# Revit family: EC-8-TY4232_Metric
name_source: partatom
category: Sprinklers
units: mm (PartAtom-declared; Revit-internal decimal feet)

## family parameters
Always vertical = Yes
Cut with Voids When Loaded = No
Maintain Annotation Orientation = No
OmniClass Number = 23.65.70.17.11.24
OmniClass Title = Fire Fighting Sprinkler Heads
Part Type = Normal
Room Calculation Point = No
Round Connector Dimension = Use Diameter
Shared = No
Work Plane-Based = No

## types (6) — shared parameters
COBie = Yes
COBie.Component.Name = Sprinklers:Pendent_SIN
COBie.Type = Yes
COBie.Type.AssetType = Fixed
COBie.Type.Category = Pr_70_55_97_84:Sprinklers
COBie.Type.DurationUnit = year
COBie.Type.Manufacturer = Tyco Fire Protection Products
COBie.Type.Material = Bronze
COBie.Type.Shape = Cylinder
COBie.Type.Size = 3/4"(DN20)
COBie.Type.WarrantyGuarantorParts = http://tycofsbp.com
Coverage = Extended
Coverage_ = Extended
K-Factor = 114.87
Manufacturer = Tyco Fire Protection Products
Manufacturer URL = www.tyco-fire.com
Material_ = Bronze
Model = EC-8
Nominal Diameter 1 = 20 mm
Orifice = Extra Large
Orifice Size = 13 mm
Outside Diameter 1 = 27 mm
Response = Quick
Response_ = Quick
SIN No = TY4232
Takeout 1 = 54 mm
Technical Data Sheet No = TFP223
zero-valued in all types: COBie.Type.NominalHeight, COBie.Type.NominalLength, COBie.Type.NominalWidth, COBie.Type.ReplacementCost, Default Elevation, Style Id

## per-type parameters (varying)
| type | COBie.Component.Description | COBie.Type.Colour | COBie.Type.Finish | COBie.Type.ModelNumber | COBie.Type.ModelReference | Description | Finish_ | Part No | Temperature Rating |
| EC-8, Recessed Pendent Sprinkler ECLH 3/4" NPT K=8.0 57°C Brass_50-801-1-135 | EC-8 Wet Pendent  57.2°C K115 DN20 NPT Br | Yellow | Natural Brass | 50-801-1-135 | EC-8 Wet Pendent  57.2°C K115 DN20 NPT Br | EC-8 Wet Pendent  57.2°C K115 DN20 NPT Br | Natural Brass | 50-801-1-135 | 57 °C |
| EC-8, Recessed Pendent Sprinkler ECLH 3/4" NPT K=8.0 68°C Brass_50-801-1-155 | EC-8 Wet Pendent  68.3°C K115 DN20 NPT Br | Yellow | Natural Brass | 50-801-1-155 | EC-8 Wet Pendent  68.3°C K115 DN20 NPT Br | EC-8 Wet Pendent  68.3°C K115 DN20 NPT Br | Natural Brass | 50-801-1-155 | 68 °C |
| EC-8, Recessed Pendent Sprinkler ECLH 3/4" NPT K=8.0 57°C White_50-801-4-135 | EC-8 Wet Pendent  57.2°C K115 DN20 NPT Wh9003 | White | Signal White | 50-801-4-135 | EC-8 Wet Pendent  57.2°C K115 DN20 NPT Wh9003 | EC-8 Wet Pendent  57.2°C K115 DN20 NPT Wh9003 | White RAL9003 | 50-801-4-135 | 57 °C |
| EC-8, Recessed Pendent Sprinkler ECLH 3/4" NPT K=8.0 68°C White_50-801-4-155 | EC-8 Wet Pendent  68.3°C K115 DN20 NPT Wh9003 | White | Signal White | 50-801-4-155 | EC-8 Wet Pendent  68.3°C K115 DN20 NPT Wh9003 | EC-8 Wet Pendent  68.3°C K115 DN20 NPT Wh9003 | White RAL9003 | 50-801-4-155 | 68 °C |
| EC-8, Recessed Pendent Sprinkler ECLH 3/4" NPT K=8.0 57°C Chrome_50-801-9-135 | EC-8 Wet Pendent  57.2°C K115 DN20 NPT Chr | Silver | Chrome Plated | 50-801-9-135 | EC-8 Wet Pendent  57.2°C K115 DN20 NPT Chr | EC-8 Wet Pendent  57.2°C K115 DN20 NPT Chr | Chrome Plated | 50-801-9-135 | 57 °C |
| EC-8, Recessed Pendent Sprinkler ECLH 3/4" NPT K=8.0 68°C Chrome_50-801-9-155 | EC-8 Wet Pendent  68.3°C K115 DN20 NPT Chr | Silver | Chrome Plated | 50-801-9-155 | EC-8 Wet Pendent  68.3°C K115 DN20 NPT Chr | EC-8 Wet Pendent  68.3°C K115 DN20 NPT Chr | Chrome Plated | 50-801-9-155 | 68 °C |

## geometry (parser evidence)
native form markers: Blend x2, Sweep x49
no freeform markers — native parametric forms only
